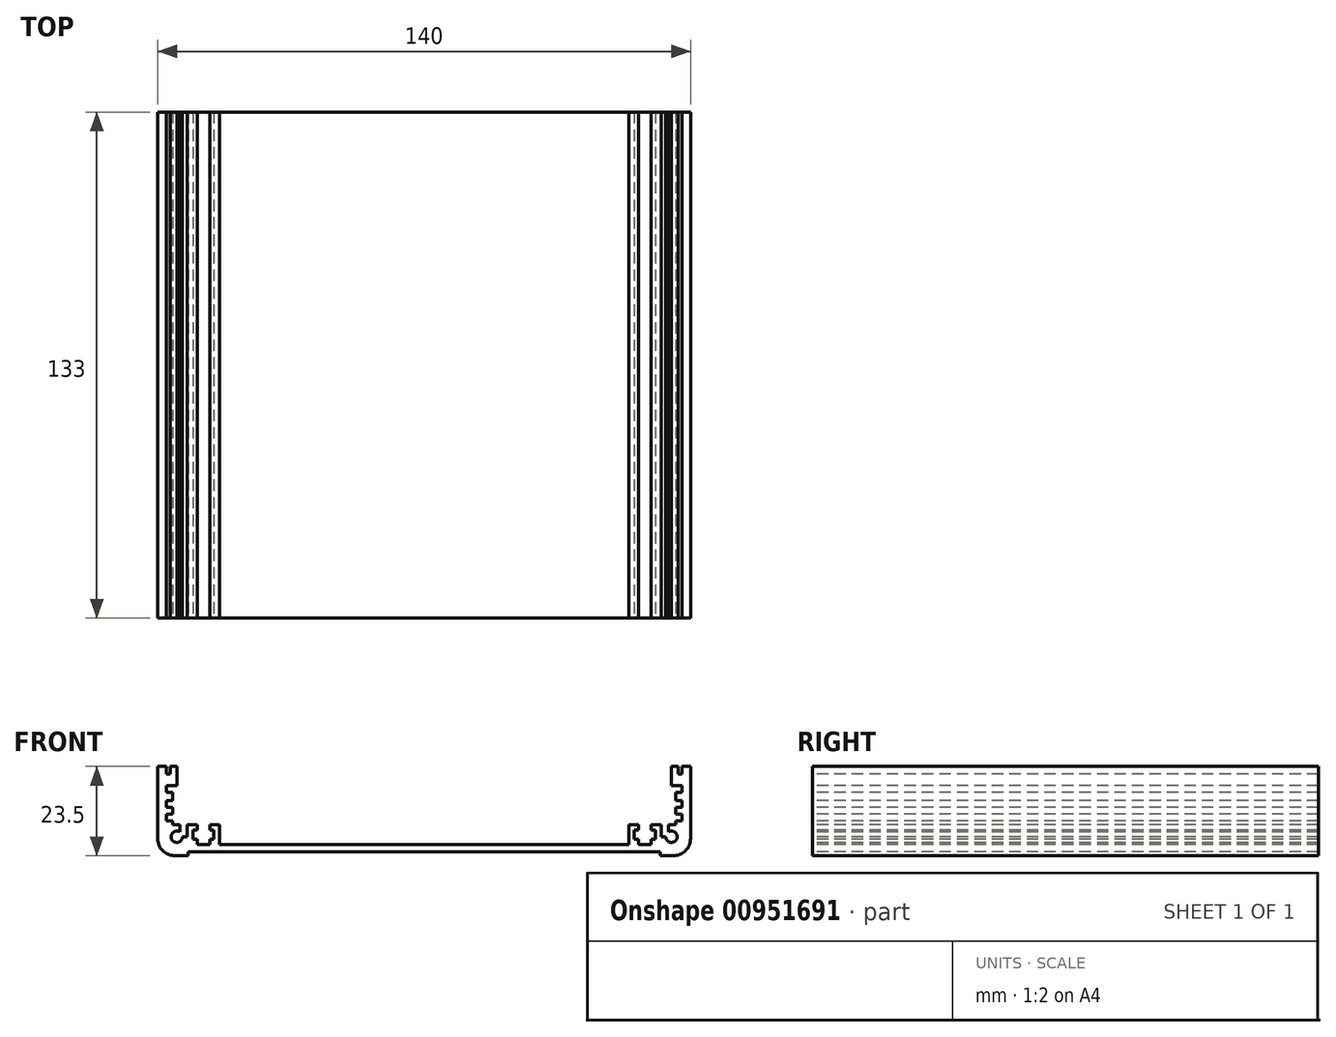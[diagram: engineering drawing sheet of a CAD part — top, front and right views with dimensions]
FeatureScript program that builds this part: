
annotation { "Feature Type Name" : "Feature", "Feature Type Description" : "" }
export const myFeature = defineFeature(function(context is Context, id is Id, definition is map)
    precondition{}
    {
        {
            var Q0;
            Q0=qCreatedBy(makeId("Front.planeOp"),FACE);
            var sketch = newSketch(context, id + "F0", { "sketchPlane" : qUnion([Q0])});
            skLineSegment(sketch, "E0.bottom", {"start": v(-65.5, 17.5) * mm, "end": v(65.5, 17.5) * mm});
            skLineSegment(sketch, "E0.top", {"start": v(-65.5, -17.5) * mm, "end": v(65.5, -17.5) * mm});
            skLineSegment(sketch, "E0.left", {"start": v(-70, 13) * mm, "end": v(-70, -13) * mm});
            skLineSegment(sketch, "E0.right", {"start": v(70, 13) * mm, "end": v(70, -13) * mm});
            skPoint(sketch, "E0.middle", {"position": v(0, 0) * mm});
            skLineSegment(sketch, "E1", {"start": v(0, 17.5) * mm, "end": v(0, -17.5) * mm, "construction": true});
            skLineSegment(sketch, "E2", {"start": v(-70, 0) * mm, "end": v(70, 0) * mm, "construction": true});
            skPoint(sketch, "E3.visualSharp", {"position": v(-70, 17.5) * mm});
            skArc(sketch, "E3.filletArc", {"start": v(-65.5, 17.5) * mm, "mid": v(-68.68, 16.18) * mm, "end": v(-70, 13) * mm});
            skPoint(sketch, "E4.visualSharp", {"position": v(70, 17.5) * mm});
            skArc(sketch, "E4.filletArc", {"start": v(70, 13) * mm, "mid": v(68.68, 16.18) * mm, "end": v(65.5, 17.5) * mm});
            skPoint(sketch, "E5.visualSharp", {"position": v(70, -17.5) * mm});
            skArc(sketch, "E5.filletArc", {"start": v(65.5, -17.5) * mm, "mid": v(68.68, -16.18) * mm, "end": v(70, -13) * mm});
            skPoint(sketch, "E6.visualSharp", {"position": v(-70, -17.5) * mm});
            skArc(sketch, "E6.filletArc", {"start": v(-70, -13) * mm, "mid": v(-68.68, -16.18) * mm, "end": v(-65.5, -17.5) * mm});
            skLineSegment(sketch, "E7.bottom", {"start": v(-62, 17.5) * mm, "end": v(62, 17.5) * mm});
            skLineSegment(sketch, "E7.top", {"start": v(-62, 16.5) * mm, "end": v(62, 16.5) * mm});
            skLineSegment(sketch, "E7.left", {"start": v(-62, 17.5) * mm, "end": v(-62, 16.5) * mm});
            skLineSegment(sketch, "E7.right", {"start": v(62, 17.5) * mm, "end": v(62, 16.5) * mm});
            skLineSegment(sketch, "E8", {"start": v(0, 16.5) * mm, "end": v(0, 17.5) * mm, "construction": true});
            skLineSegment(sketch, "E9.MirrorCS", {"start": v(62, -17.5) * mm, "end": v(62, -16.5) * mm});
            skLineSegment(sketch, "E10.MirrorCS", {"start": v(-62, -17.5) * mm, "end": v(-62, -16.5) * mm});
            skLineSegment(sketch, "E11.MirrorCS", {"start": v(-62, -16.5) * mm, "end": v(62, -16.5) * mm});
            skLineSegment(sketch, "E12.MirrorCS", {"start": v(-62, -17.5) * mm, "end": v(62, -17.5) * mm});
            skLineSegment(sketch, "E13", {"start": v(-65, 12.5) * mm, "end": v(-65, -12.5) * mm, "construction": true});
            skPoint(sketch, "E14", {"position": v(-65, 0) * mm});
            skCircle(sketch, "E15", {"center": v(-65, 12.5) * mm, "radius": 1.5 * mm});
            skCircle(sketch, "E16.MirrorC", {"center": v(-65, -12.5) * mm, "radius": 1.5 * mm});
            skCircle(sketch, "E17.MirrorC", {"center": v(65, -12.5) * mm, "radius": 1.5 * mm});
            skCircle(sketch, "E18.MirrorC", {"center": v(65, 12.5) * mm, "radius": 1.5 * mm});
            skLineSegment(sketch, "E19", {"start": v(-70, 8.95) * mm, "end": v(-55.9, 8.95) * mm, "construction": true});
            skLineSegment(sketch, "E20.bottom", {"start": v(-67.75, 9.85) * mm, "end": v(-55.35, 9.85) * mm});
            skLineSegment(sketch, "E20.top", {"start": v(-67.75, 8.05) * mm, "end": v(-55.35, 8.05) * mm});
            skLineSegment(sketch, "E20.left", {"start": v(-67.75, 9.85) * mm, "end": v(-67.75, 8.05) * mm});
            skLineSegment(sketch, "E20.right", {"start": v(-55.35, 9.85) * mm, "end": v(-55.35, 8.05) * mm});
            skPoint(sketch, "E20.middle", {"position": v(-61.55, 8.95) * mm});
            skArc(sketch, "E21", {"start": v(-65, 11) * mm, "mid": v(-64.43, 10.43) * mm, "end": v(-65, 9.85) * mm});
            skLineSegment(sketch, "E22", {"start": v(-62, 17.5) * mm, "end": v(-62, -17.5) * mm, "construction": true});
            skLineSegment(sketch, "E23.bottom", {"start": v(-62, 16.5) * mm, "end": v(-63.6, 16.5) * mm});
            skLineSegment(sketch, "E23.top", {"start": v(-62, 13.05) * mm, "end": v(-63.6, 13.05) * mm});
            skLineSegment(sketch, "E23.left", {"start": v(-62, 16.5) * mm, "end": v(-62, 13.05) * mm});
            skLineSegment(sketch, "E23.right", {"start": v(-63.6, 16.5) * mm, "end": v(-63.6, 13.05) * mm});
            skLineSegment(sketch, "E24", {"start": v(-65, 12.5) * mm, "end": v(-62, 12.5) * mm, "construction": true});
            skArc(sketch, "E25", {"start": v(-63.6, 13.05) * mm, "mid": v(-62.8, 12.5) * mm, "end": v(-62, 13.05) * mm});
            skLineSegment(sketch, "E26.bottom", {"start": v(-67.75, 8.05) * mm, "end": v(-65, 8.05) * mm});
            skLineSegment(sketch, "E26.top", {"start": v(-67.75, 6) * mm, "end": v(-65, 6) * mm});
            skLineSegment(sketch, "E26.left", {"start": v(-67.75, 8.05) * mm, "end": v(-67.75, 6) * mm});
            skLineSegment(sketch, "E26.right", {"start": v(-65, 8.05) * mm, "end": v(-65, 6) * mm});
            skLineSegment(sketch, "E27.bottom", {"start": v(-67.75, 6) * mm, "end": v(-66.75, 6) * mm});
            skLineSegment(sketch, "E27.top", {"start": v(-67.75, 4) * mm, "end": v(-66.75, 4) * mm});
            skLineSegment(sketch, "E27.left", {"start": v(-67.75, 6) * mm, "end": v(-67.75, 4) * mm});
            skLineSegment(sketch, "E27.right", {"start": v(-66.75, 6) * mm, "end": v(-66.75, 4) * mm});
            skLineSegment(sketch, "E28", {"start": v(-67.75, 6) * mm, "end": v(-70, 6) * mm});
            skLineSegment(sketch, "E29.bottom", {"start": v(-67.75, 1) * mm, "end": v(-54.85, 1) * mm});
            skLineSegment(sketch, "E29.top", {"start": v(-67.75, -0.8) * mm, "end": v(-54.85, -0.8) * mm});
            skLineSegment(sketch, "E29.left", {"start": v(-67.75, 1) * mm, "end": v(-67.75, -0.8) * mm});
            skLineSegment(sketch, "E29.right", {"start": v(-54.85, 1) * mm, "end": v(-54.85, -0.8) * mm});
            skLineSegment(sketch, "E30.bottom", {"start": v(-67.75, -3) * mm, "end": v(-55.06, -3) * mm});
            skLineSegment(sketch, "E30.top", {"start": v(-67.75, -4.8) * mm, "end": v(-55.06, -4.8) * mm});
            skLineSegment(sketch, "E30.left", {"start": v(-67.75, -3) * mm, "end": v(-67.75, -4.8) * mm});
            skLineSegment(sketch, "E30.right", {"start": v(-55.06, -3) * mm, "end": v(-55.06, -4.8) * mm});
            skLineSegment(sketch, "E31.bottom", {"start": v(-67.75, -6.5) * mm, "end": v(-54.67, -6.5) * mm});
            skLineSegment(sketch, "E31.top", {"start": v(-67.75, -8.3) * mm, "end": v(-54.67, -8.3) * mm});
            skLineSegment(sketch, "E31.left", {"start": v(-67.75, -6.5) * mm, "end": v(-67.75, -8.3) * mm});
            skLineSegment(sketch, "E31.right", {"start": v(-54.67, -6.5) * mm, "end": v(-54.67, -8.3) * mm});
            skLineSegment(sketch, "E32", {"start": v(-66.1, -0.8) * mm, "end": v(-66.1, -3) * mm});
            skLineSegment(sketch, "E33", {"start": v(-66.1, -4.8) * mm, "end": v(-66.1, -6.5) * mm});
            skLineSegment(sketch, "E34.bottom", {"start": v(-60.75, -10.7) * mm, "end": v(-55.25, -10.7) * mm});
            skLineSegment(sketch, "E34.top", {"start": v(-60.75, -13.2) * mm, "end": v(-55.25, -13.2) * mm});
            skLineSegment(sketch, "E34.left", {"start": v(-60.75, -10.7) * mm, "end": v(-60.75, -13.2) * mm});
            skLineSegment(sketch, "E34.right", {"start": v(-55.25, -10.7) * mm, "end": v(-55.25, -13.2) * mm});
            skLineSegment(sketch, "E35", {"start": v(-58, -10.7) * mm, "end": v(-58, -13.2) * mm, "construction": true});
            skLineSegment(sketch, "E36.bottom", {"start": v(-59.65, -9.4) * mm, "end": v(-56.35, -9.4) * mm});
            skLineSegment(sketch, "E36.top", {"start": v(-59.65, -14.5) * mm, "end": v(-56.35, -14.5) * mm});
            skLineSegment(sketch, "E36.left", {"start": v(-59.65, -9.4) * mm, "end": v(-59.65, -14.5) * mm});
            skLineSegment(sketch, "E36.right", {"start": v(-56.35, -9.4) * mm, "end": v(-56.35, -14.5) * mm});
            skPoint(sketch, "E36.middle", {"position": v(-58, -11.95) * mm});
            skLineSegment(sketch, "E37.bottom", {"start": v(-64.25, -12.5) * mm, "end": v(-62.25, -12.5) * mm});
            skLineSegment(sketch, "E37.top", {"start": v(-64.25, -9.4) * mm, "end": v(-62.25, -9.4) * mm});
            skLineSegment(sketch, "E37.left", {"start": v(-64.25, -12.5) * mm, "end": v(-64.25, -9.4) * mm});
            skLineSegment(sketch, "E37.right", {"start": v(-62.25, -12.5) * mm, "end": v(-62.25, -9.4) * mm});
            skLineSegment(sketch, "E38.bottom", {"start": v(-66.1, -8.3) * mm, "end": v(-64.25, -8.3) * mm});
            skLineSegment(sketch, "E38.top", {"start": v(-66.1, -9.4) * mm, "end": v(-64.25, -9.4) * mm});
            skLineSegment(sketch, "E38.left", {"start": v(-66.1, -8.3) * mm, "end": v(-66.1, -9.4) * mm});
            skLineSegment(sketch, "E38.right", {"start": v(-64.25, -8.3) * mm, "end": v(-64.25, -9.4) * mm});
            skLineSegment(sketch, "E39", {"start": v(-62.25, -9.4) * mm, "end": v(-59.65, -9.4) * mm});
            skLineSegment(sketch, "E40", {"start": v(-56.35, -9.4) * mm, "end": v(-53.75, -9.4) * mm});
            skLineSegment(sketch, "E41", {"start": v(-53.75, -9.4) * mm, "end": v(-53.75, -14.5) * mm});
            skLineSegment(sketch, "E42", {"start": v(-53.75, -14.5) * mm, "end": v(0, -14.5) * mm});
            skLineSegment(sketch, "E43", {"start": v(0, -14.5) * mm, "end": v(0, -16.5) * mm});
            skLineSegment(sketch, "E44", {"start": v(-62, 14.5) * mm, "end": v(0, 14.5) * mm});
            skLineSegment(sketch, "E45", {"start": v(0, 14.5) * mm, "end": v(0, 16.5) * mm});
            skLineSegment(sketch, "E46", {"start": v(-65, 6) * mm, "end": v(-65, 1) * mm});
            skSolve(sketch);
        }
        {
            var Q0;
            {var subQ7=sQuery(id+"F0.wireOp",EDGE,"E6.filletArc");Q0=makeQuery(id+"F0.imprint","IMPRINT",FACE,{"disambiguationData":[TD([[makeQuery(id+"F0.imprint","IMPRINT",EDGE,{"derivedFrom":subQ7}),1.0]])]});}
            extrude(context, id + "F1", {"entities" : qUnion([Q0]), "oppositeDirection" : true, "depth" : 133 * mm, "offsetDistance" : 25 * mm});
        }
        {
            var Q0;
            Q0=makeQuery(id+"F1.opExtrude","SWEPT_BODY",BODY,{"disambiguationData":[OSD([sQuery(id+"F0.wireOp",EDGE,"E0.top"),sQuery(id+"F0.wireOp",EDGE,"E0.left"),sQuery(id+"F0.wireOp",EDGE,"E6.filletArc"),sQuery(id+"F0.wireOp",EDGE,"E10.MirrorCS"),sQuery(id+"F0.wireOp",EDGE,"E11.MirrorCS"),sQuery(id+"F0.wireOp",EDGE,"E16.MirrorC"),sQuery(id+"F0.wireOp",EDGE,"E26.top"),sQuery(id+"F0.wireOp",EDGE,"E27.top"),sQuery(id+"F0.wireOp",EDGE,"E27.left"),sQuery(id+"F0.wireOp",EDGE,"E27.right"),sQuery(id+"F0.wireOp",EDGE,"E28"),sQuery(id+"F0.wireOp",EDGE,"E29.bottom"),sQuery(id+"F0.wireOp",EDGE,"E29.top"),sQuery(id+"F0.wireOp",EDGE,"E29.left"),sQuery(id+"F0.wireOp",EDGE,"E30.bottom"),sQuery(id+"F0.wireOp",EDGE,"E30.top"),sQuery(id+"F0.wireOp",EDGE,"E30.left"),sQuery(id+"F0.wireOp",EDGE,"E31.bottom"),sQuery(id+"F0.wireOp",EDGE,"E31.top"),sQuery(id+"F0.wireOp",EDGE,"E31.left"),sQuery(id+"F0.wireOp",EDGE,"E32"),sQuery(id+"F0.wireOp",EDGE,"E33"),sQuery(id+"F0.wireOp",EDGE,"E34.bottom"),sQuery(id+"F0.wireOp",EDGE,"E34.top"),sQuery(id+"F0.wireOp",EDGE,"E34.left"),sQuery(id+"F0.wireOp",EDGE,"E34.right"),sQuery(id+"F0.wireOp",EDGE,"E36.top"),sQuery(id+"F0.wireOp",EDGE,"E36.left"),sQuery(id+"F0.wireOp",EDGE,"E36.right"),sQuery(id+"F0.wireOp",EDGE,"E37.bottom"),sQuery(id+"F0.wireOp",EDGE,"E37.left"),sQuery(id+"F0.wireOp",EDGE,"E37.right"),sQuery(id+"F0.wireOp",EDGE,"E38.top"),sQuery(id+"F0.wireOp",EDGE,"E38.left"),sQuery(id+"F0.wireOp",EDGE,"E39"),sQuery(id+"F0.wireOp",EDGE,"E40"),sQuery(id+"F0.wireOp",EDGE,"E41"),sQuery(id+"F0.wireOp",EDGE,"E42"),sQuery(id+"F0.wireOp",EDGE,"E43"),sQuery(id+"F0.wireOp",EDGE,"E46")])]});
            var Q1;
            Q1=makeQuery(id+"F1.opExtrude","SWEPT_FACE",FACE,{"disambiguationData":[OSD([sQuery(id+"F0.wireOp",EDGE,"E43")])]});
            mirror(context, id + "F2", {"operationType" : NewBodyOperationType.ADD, "entities" : qUnion([Q0]), "mirrorPlane" : qUnion([Q1])});
        }
    });
